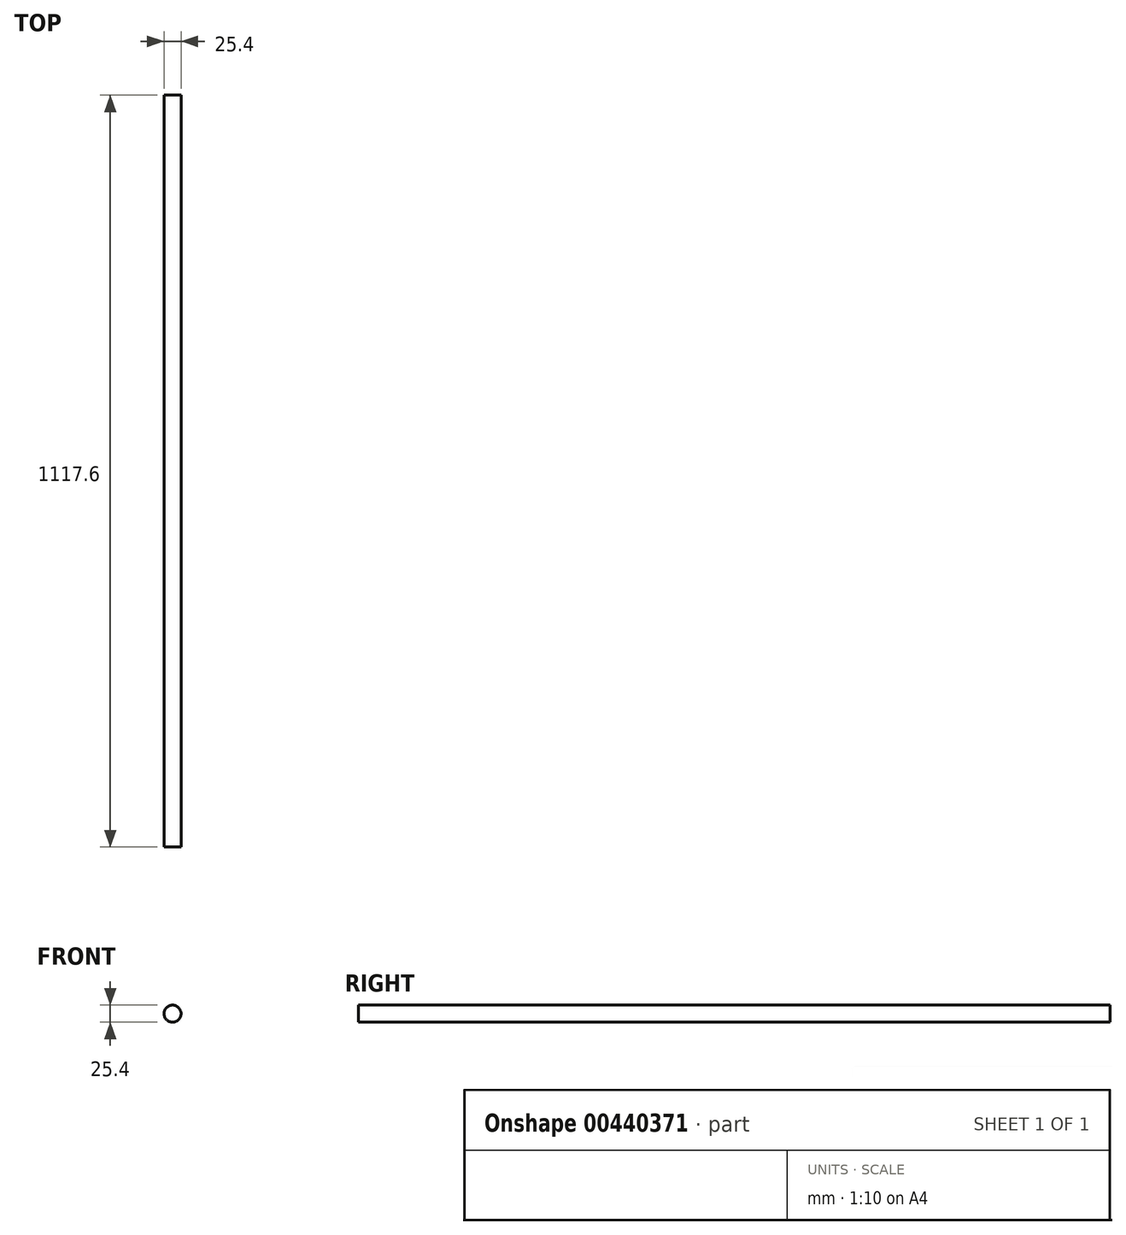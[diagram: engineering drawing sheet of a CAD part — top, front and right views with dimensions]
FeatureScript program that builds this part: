
annotation { "Feature Type Name" : "Feature", "Feature Type Description" : "" }
export const myFeature = defineFeature(function(context is Context, id is Id, definition is map)
    precondition{}
    {
        {
            var Q0;
            Q0=qCreatedBy(makeId("Front.planeOp"),FACE);
            var sketch = newSketch(context, id + "F0", { "sketchPlane" : qUnion([Q0])});
            skCircle(sketch, "E0", {"center": v(0, 0) * mm, "radius": 12.7 * mm});
            skSolve(sketch);
        }
        {
            var Q0;
            Q0=makeQuery(id+"F0.imprint","IMPRINT",FACE,{"disambiguationData":[TD([[makeQuery(id+"F0.imprint","IMPRINT",EDGE,{"derivedFrom":sQuery(id+"F0.wireOp",EDGE,"E0")}),1.0]])]});
            extrude(context, id + "F1", {"entities" : qUnion([Q0]), "endBound" : BoundingType.SYMMETRIC, "depth" : 1117.6 * mm});
        }
    });
